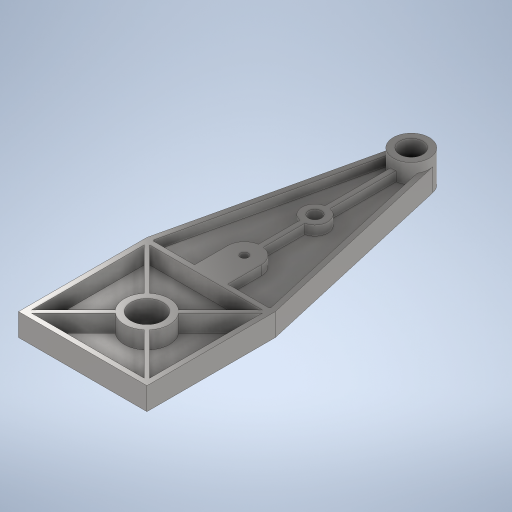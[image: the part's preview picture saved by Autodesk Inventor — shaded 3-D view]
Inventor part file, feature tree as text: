
AUTODESK INVENTOR PART (.ipt)
format: ipt  version: 2024 (Build 280153000, 153)  size: 398,848 bytes
history: native  units: mm
features: sketch x6, extrude x6, plane x2, mirror x2, hole x2, fillet x1
ambient origin geometry x8: Origin, YZ Plane, XZ Plane, XY Plane, X Axis, Y Axis, Z Axis, Center Point
bodies: Volumenkörper1 (feature_tree)
feature tree (19):
  sketch  "Skizze1"  dims[d0=56.0mm d1=36.0mm]
  extrude  "Extrusion1"  Depth=36.0mm
  extrude  "Extrusion2"  Depth=200.0mm
  sketch  "Skizze6"  dims[d2=518.0mm d3=200.0mm]
  plane  "Arbeitsebene1"
  extrude  "Extrusion8"  Depth=200.0mm
  extrude  "Extrusion9"  Depth=35.0mm TaperAngle=0.0deg
  mirror  "Spiegeln2"
  plane  "Arbeitsebene2"
  mirror  "Spiegeln3"
  extrude  "Extrusion10"  Depth=100.0mm
  extrude  "Extrusion11"  Depth=8.0mm
  hole  "Bohrung1"  [1 undecoded]
  hole  "Bohrung2"  [1 undecoded]
  fillet  "Rundung1"  [1 undecoded]
  sketch  "Skizze7"  dims[d4=200.0mm d8=318.0mm]
  sketch  "Skizze8"  dims[d9=50.0mm d10=0.0mm d11=35.0mm d12=0.0mm]
  sketch  "Skizze9"  dims[d36=100.0mm d37=70.0mm]
  sketch  "Skizze10"  dims[d38=8.0mm d39=8.0mm d40=8.0mm d41=6.0mm d42=45.0deg d43=6.0mm d46=0.0mm d47=6.0mm d48=27.0mm d49=0.0mm d50=27.0mm d51=0.0mm d52=100.0mm d53=50.0mm d54=100.0mm d55=27.0mm d56=0.0mm d57=8.0mm d58=8.0mm d60=8.0mm d64=260.0mm d65=26.0mm d66=40.0mm d67=110.0mm d68=8.0mm d69=15.0mm d70=0.0mm d71=12.0mm d72=6.0mm d73=7.0mm d74=1.0mm d75=90.0deg d76=8.0mm d77=20.594885mm d78=20.0mm d79=6.0mm d80=4.0mm d81=2.0mm d82=90.0deg d83=8.0mm d84=0.0mm d85=2.0mm d27=0.5mm d28=0.872665mm d29=0.5mm d30=0.872665mm]
note: 3 required parameter values undecoded (feature->parameter linkage not recoverable at this tier; creation-order binding heuristic only, values carry confidence <= 0.55)
